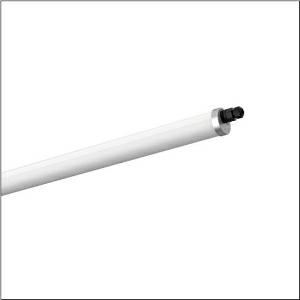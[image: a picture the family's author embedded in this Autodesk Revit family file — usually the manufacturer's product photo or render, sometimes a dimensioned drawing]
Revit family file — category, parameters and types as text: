
# Revit family: monsun_r__31_tube_51ft107n4a0a_c9dd
name_source: partatom
category: Lighting Fixtures
units: mm (PartAtom-declared; Revit-internal decimal feet)

## family parameters
Cut with Voids When Loaded = No
Host = Face
Light Source = No
Part Type = Normal
Room Calculation Point = No
Round Connector Dimension = Use Diameter
Shared = No

## types (1)
- Monsun® 31 Tube (1 x LED, 10000 lm, 58 W, 4000K)
    Apparent Load = 58 VA
    CIE Flux Codes = 42 71 90 91 100
    Color Rendering = 80
    Color Temperature = 4000K
    Default Elevation = 1800 mm
    Description = Monsun® 31 Tube, tubular luminaire, primary optical cover: diffuser, of PMMA, light emission: direct distribution, primary light characteristic: symmetric, installation type: suspended mounting, surface-mounted, LED, rated luminous flux: 10.000lm, luminous efficacy: 160lm/W, light colour: 840, colour temperature: 4000K, control gear: ON/OFF, with with 1 terminal, 3-pole, max. 2.5mm², through-wiring: 3x 1.5mm², mains connection: 220..240V, AC, 50/60Hz, rated input power: 58W, housing, cylindrical, of PMMA, semi-transparent, matt white, with luminaire and ceiling fastening, V4A, mounting with brackets of stainless steel, length: 1.560mm, diameter: 75mm, end cap, of stainless steel (V4A), protection rating (complete): IP67/IP69K, insulation class (complete): insulation class I (protective earthing), certification: CE, UKCA, impact resistance: IK07, permissible operating ambient temperature: -20..+40°C, corresponds to IFS (International Featured Standards) requirements for safety and quality in the food industry, usage in unprotected outdoor areas possible with horizontal mounting, contact your sales advisor before using the luminaires in applications with unclear chemical exposure, large temperature fluctuations or condensation-forming humidity, packaging unit: 1 piece
    Height = 83 mm
    Lamp = 1 x LED
    Lamp Light Flux = 10000 lm
    Lamp Power = 58 W
    Lamp count = 1
    Length = 1560 mm
    Luminous efficacy = 172 lm/W
    Manufacturer = Siteco
    ModVariant = No
    Model = 51FT107N4A0A
    Mounting Place = Ceiling
    Mounting Type = Pendant
    Number of Poles = 1
    OnlyDefault = Yes
    Power Factor = 1
    Product Name = Monsun® 31 Tube
    Product group = tubular luminaire
    ProductGroupID = 907
    Protection Class = Protection class I
    RLX_Detail_Level = 1
    RLX_Emergency_Light_Flux = 0 lm
    RLX_Emergency_Type = 0
    RLX_Emergency_Type_DB = No
    RlxData = <blob elided: 25333 chars, md5=544fa88e>
    Socket = socket
    Standby Power = 0 W
    System Light Flux = 10000 lm
    System Power = 58 W
    Type Comments = Product without accessories
    Type Image = l_1228461.jpg
    URL = http://relux.com
    VarID = ---
    Voltage = 0 V
    Weight = 0.00 kg
    Width = 75 mm

## geometry (parser evidence)
native form markers: Blend x4, Sweep x13
no freeform markers — native parametric forms only
